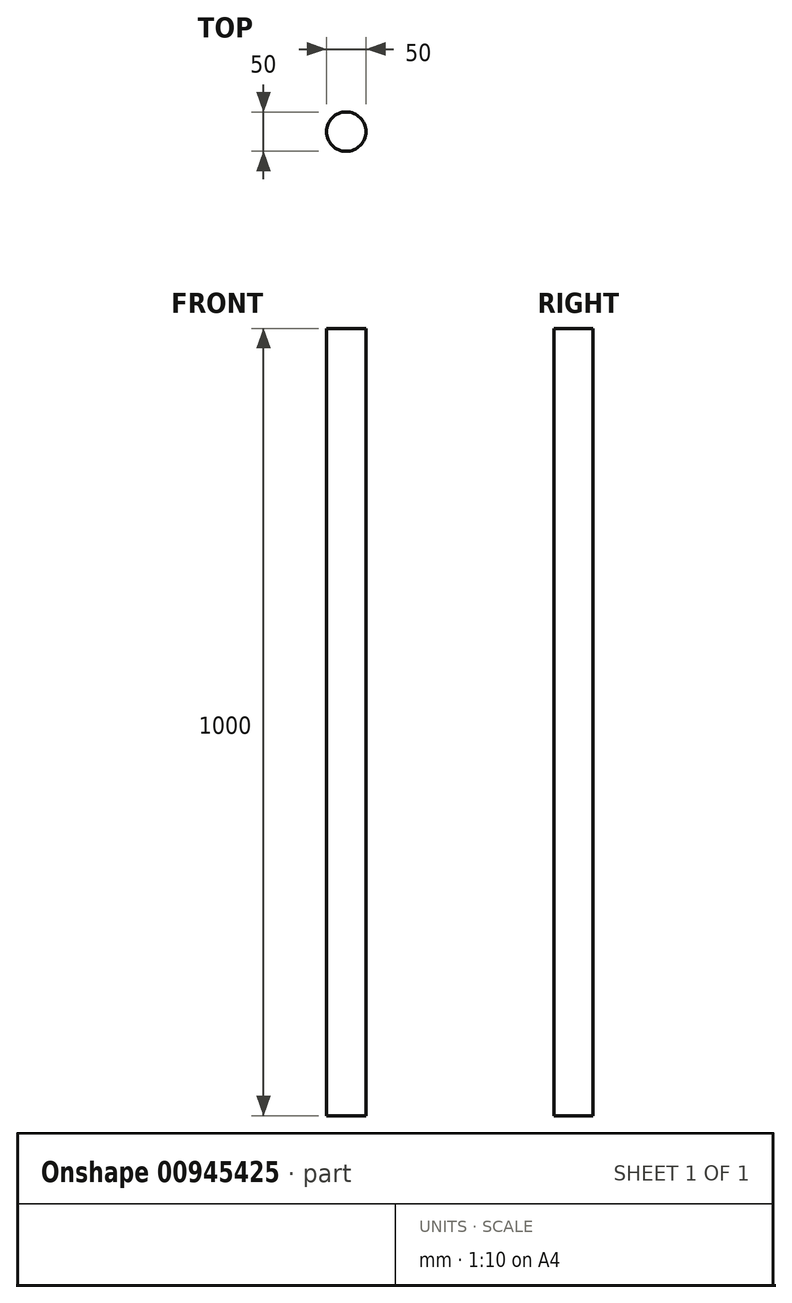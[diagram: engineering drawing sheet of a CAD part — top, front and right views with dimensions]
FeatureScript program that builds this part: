
annotation { "Feature Type Name" : "Feature", "Feature Type Description" : "" }
export const myFeature = defineFeature(function(context is Context, id is Id, definition is map)
    precondition{}
    {
        {
            var Q0;
            Q0=qCreatedBy(makeId("Top.planeOp"),FACE);
            var sketch = newSketch(context, id + "F0", { "sketchPlane" : qUnion([Q0])});
            skCircle(sketch, "E0", {"center": v(0, 0) * mm, "radius": 25 * mm});
            skSolve(sketch);
        }
        {
            var Q0;
            Q0=sQuery(id+"F0.wireOp",EDGE,"E0");
            extrude(context, id + "F1", {"bodyType" : ToolBodyType.SURFACE, "surfaceEntities" : qUnion([Q0]), "depth" : 1000 * mm, "offsetDistance" : 25.4 * mm});
        }
    });
